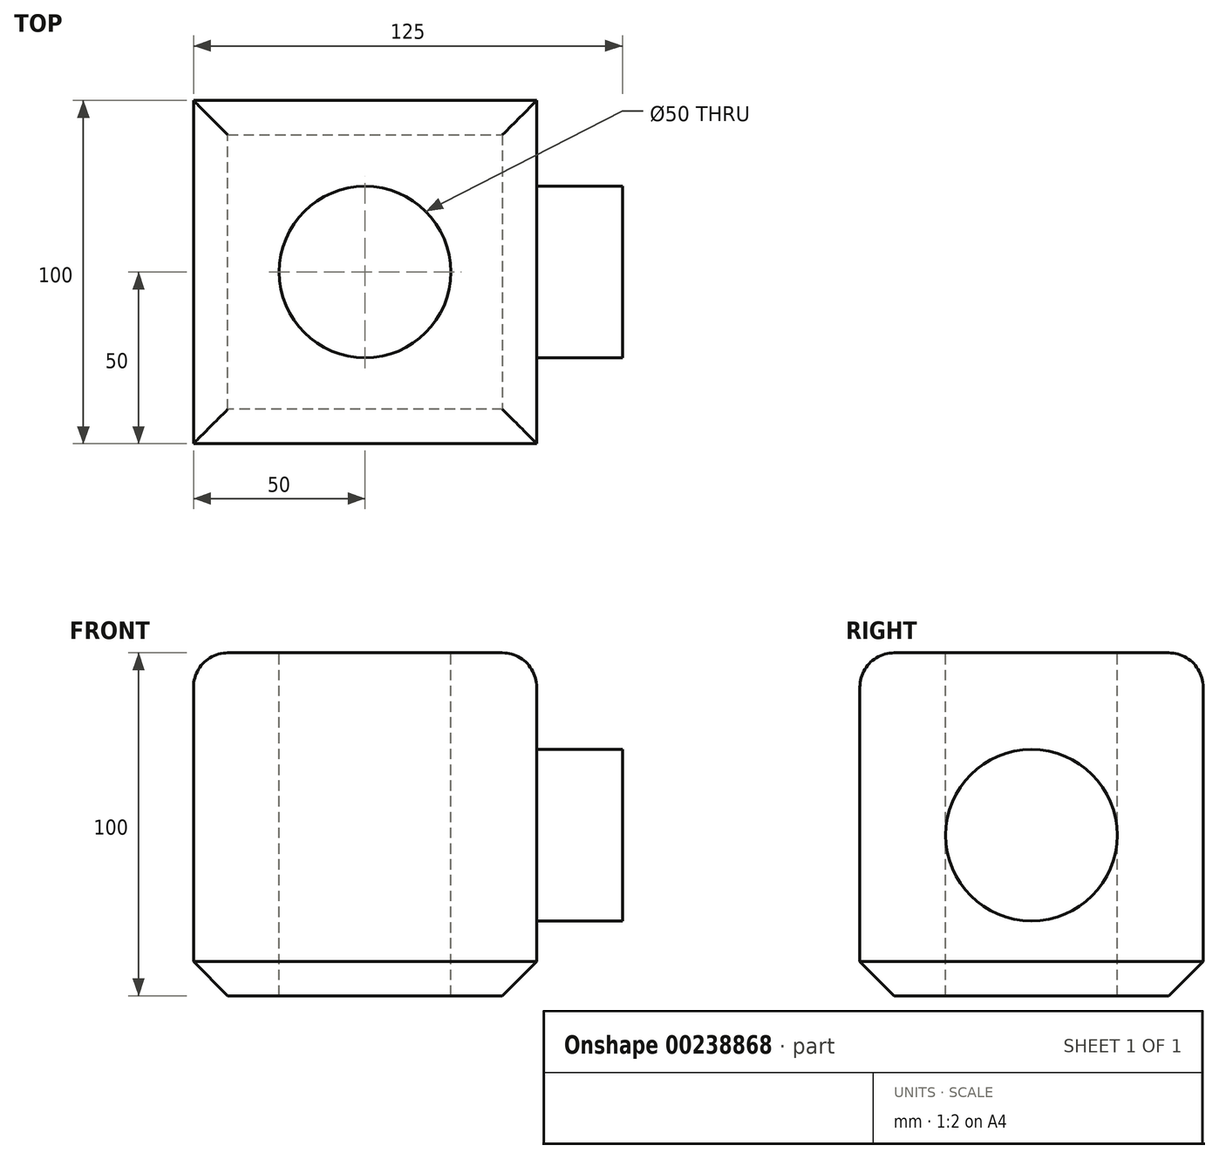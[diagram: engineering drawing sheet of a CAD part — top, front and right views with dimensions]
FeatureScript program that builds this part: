
annotation { "Feature Type Name" : "Feature", "Feature Type Description" : "" }
export const myFeature = defineFeature(function(context is Context, id is Id, definition is map)
    precondition{}
    {
        {
            var Q0;
            Q0=qCreatedBy(makeId("Top.planeOp"),FACE);
            var sketch = newSketch(context, id + "F0", { "sketchPlane" : qUnion([Q0])});
            skLineSegment(sketch, "E0.bottom", {"start": v(50, -50) * mm, "end": v(-50, -50) * mm});
            skLineSegment(sketch, "E0.top", {"start": v(50, 50) * mm, "end": v(-50, 50) * mm});
            skLineSegment(sketch, "E0.left", {"start": v(50, -50) * mm, "end": v(50, 50) * mm});
            skLineSegment(sketch, "E0.right", {"start": v(-50, -50) * mm, "end": v(-50, 50) * mm});
            skSolve(sketch);
        }
        {
            var Q0;
            Q0 = qSketchRegion(id + "F0", true);
            extrude(context, id + "F1", {"entities" : qUnion([Q0]), "depth" : 100 * mm});
        }
        {
            var Q0;
            Q0=makeQuery(id+"F1.opExtrude","CAP_EDGE",EDGE,{"disambiguationData":[OSD([sQuery(id+"F0.wireOp",EDGE,"E0.right")])],"isStart":false});
            var Q1;
            Q1=makeQuery(id+"F1.opExtrude","CAP_EDGE",EDGE,{"disambiguationData":[OSD([sQuery(id+"F0.wireOp",EDGE,"E0.bottom")])],"isStart":false});
            var Q2;
            Q2=makeQuery(id+"F1.opExtrude","CAP_EDGE",EDGE,{"disambiguationData":[OSD([sQuery(id+"F0.wireOp",EDGE,"E0.left")])],"isStart":false});
            var Q3;
            Q3=makeQuery(id+"F1.opExtrude","CAP_EDGE",EDGE,{"disambiguationData":[OSD([sQuery(id+"F0.wireOp",EDGE,"E0.top")])],"isStart":false});
            fillet(context, id + "F2", {"entities" : qUnion([Q0, Q1, Q2, Q3]), "radius" : 10 * mm, "tangentPropagation" : true, "allowEdgeOverflow" : false});
        }
        {
            var Q0;
            Q0=makeQuery(id+"F1.opExtrude","CAP_FACE",FACE,{"disambiguationData":[OSD([sQuery(id+"F0.wireOp",EDGE,"E0.bottom"),sQuery(id+"F0.wireOp",EDGE,"E0.top"),sQuery(id+"F0.wireOp",EDGE,"E0.left"),sQuery(id+"F0.wireOp",EDGE,"E0.right")])],"isStart":true});
            chamfer(context, id + "F3", {"entities" : qUnion([Q0]), "width" : 10 * mm, "tangentPropagation" : true});
        }
        {
            var Q0;
            Q0=makeQuery(id+"F1.opExtrude","CAP_FACE",FACE,{"disambiguationData":[OSD([sQuery(id+"F0.wireOp",EDGE,"E0.bottom"),sQuery(id+"F0.wireOp",EDGE,"E0.top"),sQuery(id+"F0.wireOp",EDGE,"E0.left"),sQuery(id+"F0.wireOp",EDGE,"E0.right")])],"isStart":false});
            var sketch = newSketch(context, id + "F4", { "sketchPlane" : qUnion([Q0])});
            skCircle(sketch, "E1", {"center": v(0, 0) * mm, "radius": 25 * mm});
            skSolve(sketch);
        }
        {
            var Q0;
            Q0=makeQuery(id+"F4.imprint","IMPRINT",FACE,{"disambiguationData":[TD([[makeQuery(id+"F4.imprint","IMPRINT",EDGE,{"derivedFrom":sQuery(id+"F4.wireOp",EDGE,"E1")}),1.0]])]});
            extrude(context, id + "F5", {"entities" : qUnion([Q0]), "operationType" : NewBodyOperationType.REMOVE, "oppositeDirection" : true, "depth" : 100 * mm});
        }
        {
            var Q0;
            Q0=makeQuery(id+"F1.opExtrude","SWEPT_FACE",FACE,{"disambiguationData":[OSD([sQuery(id+"F0.wireOp",EDGE,"E0.left")])]});
            var sketch = newSketch(context, id + "F6", { "sketchPlane" : qUnion([Q0])});
            skCircle(sketch, "E2", {"center": v(0, 46.82) * mm, "radius": 25 * mm});
            skSolve(sketch);
        }
        {
            var Q0;
            Q0=makeQuery(id+"F6.imprint","IMPRINT",FACE,{"disambiguationData":[TD([[makeQuery(id+"F6.imprint","IMPRINT",EDGE,{"derivedFrom":sQuery(id+"F6.wireOp",EDGE,"E2")}),1.0]])]});
            extrude(context, id + "F7", {"entities" : qUnion([Q0]), "operationType" : NewBodyOperationType.ADD, "depth" : 25 * mm});
        }
    });
